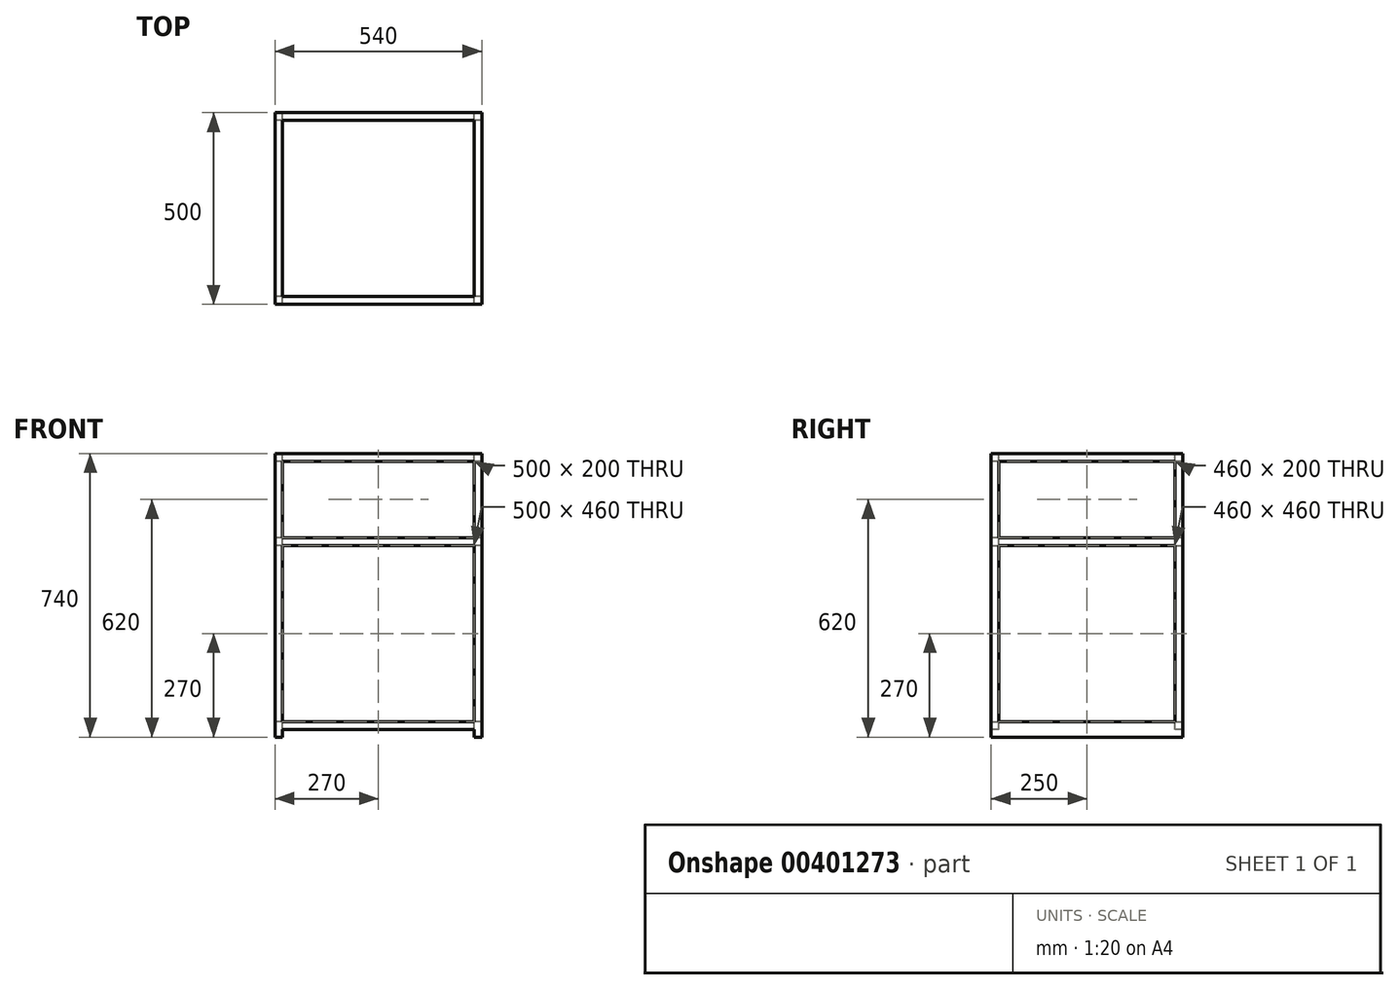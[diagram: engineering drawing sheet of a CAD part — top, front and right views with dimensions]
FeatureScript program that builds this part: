
annotation { "Feature Type Name" : "Feature", "Feature Type Description" : "" }
export const myFeature = defineFeature(function(context is Context, id is Id, definition is map)
    precondition{}
    {
        {
            var Q0;
            Q0=qCreatedBy(makeId("Top.planeOp"),FACE);
            var sketch = newSketch(context, id + "F0", { "sketchPlane" : qUnion([Q0])});
            skLineSegment(sketch, "E0.bottom", {"start": v(270, 250) * mm, "end": v(-270, 250) * mm});
            skLineSegment(sketch, "E0.top", {"start": v(270, -250) * mm, "end": v(-270, -250) * mm});
            skLineSegment(sketch, "E0.left", {"start": v(270, 250) * mm, "end": v(270, -250) * mm});
            skLineSegment(sketch, "E0.right", {"start": v(-270, 250) * mm, "end": v(-270, -250) * mm});
            skPoint(sketch, "E0.middle", {"position": v(0, 0) * mm});
            skSolve(sketch);
        }
        {
            var Q0;
            Q0=makeQuery(id+"F0.imprint","IMPRINT",FACE,{"disambiguationData":[TD([[makeQuery(id+"F0.imprint","IMPRINT",EDGE,{"derivedFrom":sQuery(id+"F0.wireOp",EDGE,"E0.bottom")}),1.0]])]});
            extrude(context, id + "F1", {"entities" : qUnion([Q0]), "depth" : 700 * mm, "hasSecondDirection" : true, "secondDirectionOppositeDirection" : true, "secondDirectionDepth" : 40 * mm});
        }
        {
            var Q0;
            Q0=makeQuery(id+"F1.opExtrude","SWEPT_FACE",FACE,{"disambiguationData":[OSD([sQuery(id+"F0.wireOp",EDGE,"E0.top")])]});
            var sketch = newSketch(context, id + "F2", { "sketchPlane" : qUnion([Q0])});
            skLineSegment(sketch, "E1.bottom", {"start": v(-270, -40) * mm, "end": v(270, -40) * mm});
            skLineSegment(sketch, "E1.top", {"start": v(-270, -20) * mm, "end": v(270, -20) * mm});
            skLineSegment(sketch, "E1.left", {"start": v(-270, -40) * mm, "end": v(-270, -20) * mm});
            skLineSegment(sketch, "E1.right", {"start": v(270, -40) * mm, "end": v(270, -20) * mm, "construction": true});
            skLineSegment(sketch, "E2.bottom", {"start": v(-270, -40) * mm, "end": v(-250, -40) * mm, "construction": true});
            skLineSegment(sketch, "E2.top", {"start": v(-270, -20) * mm, "end": v(-250, -20) * mm, "construction": true});
            skLineSegment(sketch, "E2.left", {"start": v(-270, -40) * mm, "end": v(-270, -20) * mm, "construction": true});
            skLineSegment(sketch, "E2.right", {"start": v(-250, -40) * mm, "end": v(-250, -20) * mm});
            skLineSegment(sketch, "E3.bottom", {"start": v(270, -40) * mm, "end": v(250, -40) * mm});
            skLineSegment(sketch, "E3.top", {"start": v(270, -20) * mm, "end": v(250, -20) * mm});
            skLineSegment(sketch, "E3.left", {"start": v(270, -40) * mm, "end": v(270, -20) * mm});
            skLineSegment(sketch, "E3.right", {"start": v(250, -40) * mm, "end": v(250, -20) * mm});
            skSolve(sketch);
        }
        {
            var Q0;
            {var subQ2=sQuery(id+"F2.wireOp",EDGE,"E2.right");Q0=makeQuery(id+"F2.imprint","IMPRINT",FACE,{"disambiguationData":[TD([[makeQuery(id+"F2.imprint","IMPRINT",EDGE,{"derivedFrom":subQ2}),-1.0]])]});}
            extrude(context, id + "F3", {"entities" : qUnion([Q0]), "operationType" : NewBodyOperationType.REMOVE, "endBound" : BoundingType.THROUGH_ALL, "oppositeDirection" : true, "depth" : 25 * mm});
        }
        {
            var Q0;
            Q0=makeQuery(id+"F1.opExtrude","SWEPT_FACE",FACE,{"disambiguationData":[OSD([sQuery(id+"F0.wireOp",EDGE,"E0.top")])]});
            var sketch = newSketch(context, id + "F4", { "sketchPlane" : qUnion([Q0])});
            skLineSegment(sketch, "E4.bottom", {"start": v(-250, 680) * mm, "end": v(250, 680) * mm});
            skLineSegment(sketch, "E4.top", {"start": v(-250, 480) * mm, "end": v(250, 480) * mm});
            skLineSegment(sketch, "E4.left", {"start": v(-250, 680) * mm, "end": v(-250, 480) * mm});
            skLineSegment(sketch, "E4.right", {"start": v(250, 680) * mm, "end": v(250, 480) * mm});
            skSolve(sketch);
        }
        {
            var Q0;
            Q0=makeQuery(id+"F4.imprint","IMPRINT",FACE,{"disambiguationData":[TD([[makeQuery(id+"F4.imprint","IMPRINT",EDGE,{"derivedFrom":sQuery(id+"F4.wireOp",EDGE,"E4.bottom")}),-1.0]])]});
            extrude(context, id + "F5", {"entities" : qUnion([Q0]), "operationType" : NewBodyOperationType.REMOVE, "endBound" : BoundingType.THROUGH_ALL, "oppositeDirection" : true, "depth" : 25 * mm});
        }
        {
            var Q0;
            Q0=makeQuery(id+"F1.opExtrude","SWEPT_FACE",FACE,{"disambiguationData":[OSD([sQuery(id+"F0.wireOp",EDGE,"E0.right")])]});
            var sketch = newSketch(context, id + "F6", { "sketchPlane" : qUnion([Q0])});
            skLineSegment(sketch, "E5.bottom", {"start": v(-230, 680) * mm, "end": v(230, 680) * mm});
            skLineSegment(sketch, "E5.top", {"start": v(-230, 480) * mm, "end": v(230, 480) * mm});
            skLineSegment(sketch, "E5.left", {"start": v(-230, 680) * mm, "end": v(-230, 480) * mm});
            skLineSegment(sketch, "E5.right", {"start": v(230, 680) * mm, "end": v(230, 480) * mm});
            skSolve(sketch);
        }
        {
            var Q0;
            Q0=qSketchRegion(id+"F6",true);
            extrude(context, id + "F7", {"entities" : qUnion([Q0]), "operationType" : NewBodyOperationType.REMOVE, "endBound" : BoundingType.THROUGH_ALL, "oppositeDirection" : true, "depth" : 25 * mm});
        }
        {
            var Q0;
            Q0=makeQuery(id+"F1.opExtrude","CAP_FACE",FACE,{"disambiguationData":[OSD([sQuery(id+"F0.wireOp",EDGE,"E0.bottom"),sQuery(id+"F0.wireOp",EDGE,"E0.top"),sQuery(id+"F0.wireOp",EDGE,"E0.left"),sQuery(id+"F0.wireOp",EDGE,"E0.right")])],"isStart":false});
            var sketch = newSketch(context, id + "F8", { "sketchPlane" : qUnion([Q0])});
            skLineSegment(sketch, "E6.bottom", {"start": v(-250, -230) * mm, "end": v(250, -230) * mm});
            skLineSegment(sketch, "E6.top", {"start": v(-250, 230) * mm, "end": v(250, 230) * mm});
            skLineSegment(sketch, "E6.left", {"start": v(-250, -230) * mm, "end": v(-250, 230) * mm});
            skLineSegment(sketch, "E6.right", {"start": v(250, -230) * mm, "end": v(250, 230) * mm});
            skPoint(sketch, "E6.middle", {"position": v(0, 0) * mm});
            skSolve(sketch);
        }
        {
            var Q0;
            Q0=makeQuery(id+"F8.imprint","IMPRINT",FACE,{"disambiguationData":[TD([[makeQuery(id+"F8.imprint","IMPRINT",EDGE,{"derivedFrom":sQuery(id+"F8.wireOp",EDGE,"E6.bottom")}),1.0]])]});
            extrude(context, id + "F9", {"entities" : qUnion([Q0]), "operationType" : NewBodyOperationType.REMOVE, "endBound" : BoundingType.THROUGH_ALL, "oppositeDirection" : true, "depth" : 25 * mm});
        }
        {
            var Q0;
            Q0=makeQuery(id+"F1.opExtrude","SWEPT_FACE",FACE,{"disambiguationData":[OSD([sQuery(id+"F0.wireOp",EDGE,"E0.bottom")])]});
            var sketch = newSketch(context, id + "F10", { "sketchPlane" : qUnion([Q0])});
            skLineSegment(sketch, "E7.bottom", {"start": v(-250, 460) * mm, "end": v(250, 460) * mm});
            skLineSegment(sketch, "E7.top", {"start": v(-250, 0) * mm, "end": v(250, 0) * mm});
            skLineSegment(sketch, "E7.left", {"start": v(-250, 460) * mm, "end": v(-250, 0) * mm});
            skLineSegment(sketch, "E7.right", {"start": v(250, 460) * mm, "end": v(250, 0) * mm});
            skSolve(sketch);
        }
        {
            var Q0;
            Q0=makeQuery(id+"F10.imprint","IMPRINT",FACE,{"disambiguationData":[TD([[makeQuery(id+"F10.imprint","IMPRINT",EDGE,{"derivedFrom":sQuery(id+"F10.wireOp",EDGE,"E7.bottom")}),-1.0]])]});
            extrude(context, id + "F11", {"entities" : qUnion([Q0]), "operationType" : NewBodyOperationType.REMOVE, "endBound" : BoundingType.THROUGH_ALL, "oppositeDirection" : true, "depth" : 25 * mm});
        }
        {
            var Q0;
            Q0=makeQuery(id+"F1.opExtrude","SWEPT_FACE",FACE,{"disambiguationData":[OSD([sQuery(id+"F0.wireOp",EDGE,"E0.right")])]});
            var sketch = newSketch(context, id + "F12", { "sketchPlane" : qUnion([Q0])});
            skLineSegment(sketch, "E8.bottom", {"start": v(-230, 460) * mm, "end": v(230, 460) * mm});
            skLineSegment(sketch, "E8.top", {"start": v(-230, 0) * mm, "end": v(230, 0) * mm});
            skLineSegment(sketch, "E8.left", {"start": v(-230, 460) * mm, "end": v(-230, 0) * mm});
            skLineSegment(sketch, "E8.right", {"start": v(230, 460) * mm, "end": v(230, 0) * mm});
            skSolve(sketch);
        }
        {
            var Q0;
            Q0=qSketchRegion(id+"F12",true);
            extrude(context, id + "F13", {"entities" : qUnion([Q0]), "operationType" : NewBodyOperationType.REMOVE, "endBound" : BoundingType.THROUGH_ALL, "oppositeDirection" : true, "depth" : 25 * mm});
        }
    });
